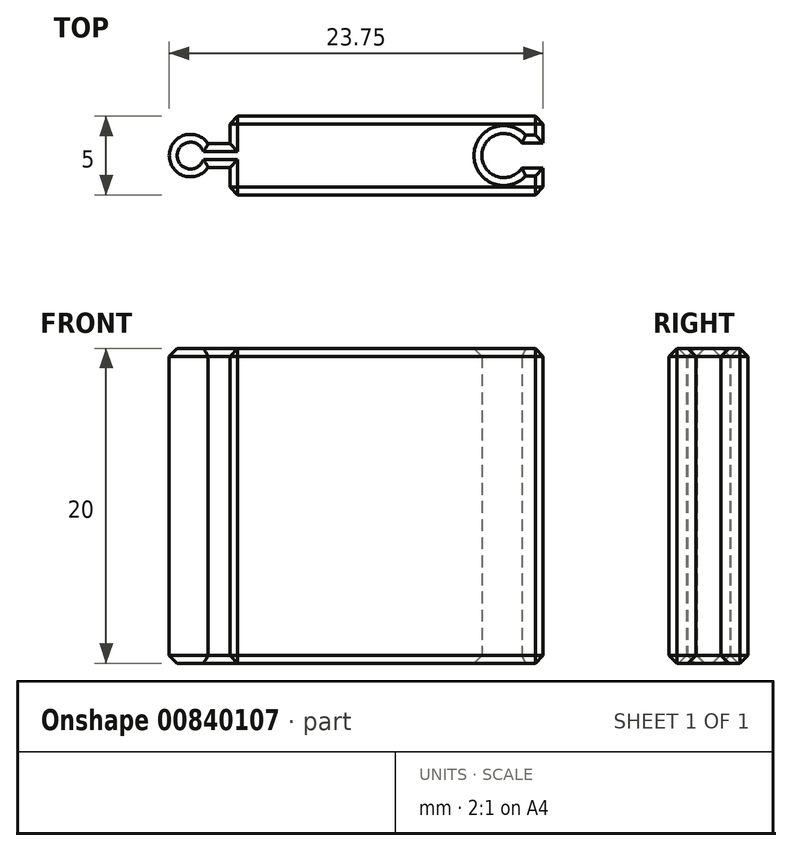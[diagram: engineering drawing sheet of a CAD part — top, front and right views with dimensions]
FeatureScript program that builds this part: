
annotation { "Feature Type Name" : "Feature", "Feature Type Description" : "" }
export const myFeature = defineFeature(function(context is Context, id is Id, definition is map)
    precondition{}
    {
        {
            var Q0;
            Q0=qCreatedBy(makeId("Top.planeOp"),FACE);
            var sketch = newSketch(context, id + "F0", { "sketchPlane" : qUnion([Q0])});
            skLineSegment(sketch, "E0.bottom", {"start": v(-9.95, 2.5) * mm, "end": v(9.95, 2.5) * mm});
            skLineSegment(sketch, "E0.top", {"start": v(-9.95, -2.5) * mm, "end": v(9.95, -2.5) * mm});
            skLineSegment(sketch, "E0.left", {"start": v(-9.95, 2.5) * mm, "end": v(-9.95, -2.5) * mm});
            skLineSegment(sketch, "E0.right", {"start": v(9.95, 2.5) * mm, "end": v(9.95, -2.5) * mm});
            skPoint(sketch, "E0.middle", {"position": v(0, 0) * mm});
            skLineSegment(sketch, "E1", {"start": v(-9.95, 0) * mm, "end": v(-12.45, 0) * mm});
            skCircle(sketch, "E2", {"center": v(-12.45, 0) * mm, "radius": 1.35 * mm});
            skLineSegment(sketch, "E3.bottom", {"start": v(-9.95, 0.75) * mm, "end": v(-12.45, 0.75) * mm});
            skLineSegment(sketch, "E3.top", {"start": v(-9.95, -0.75) * mm, "end": v(-12.45, -0.75) * mm});
            skLineSegment(sketch, "E3.left", {"start": v(-9.95, 0.75) * mm, "end": v(-9.95, -0.75) * mm});
            skLineSegment(sketch, "E3.right", {"start": v(-12.45, 0.75) * mm, "end": v(-12.45, -0.75) * mm});
            skPoint(sketch, "E3.middle", {"position": v(-11.2, 0) * mm});
            skLineSegment(sketch, "E4", {"start": v(9.95, 0) * mm, "end": v(7.45, 0) * mm});
            skCircle(sketch, "E5", {"center": v(7.45, 0) * mm, "radius": 1.4 * mm});
            skLineSegment(sketch, "E6.bottom", {"start": v(9.95, 0.8) * mm, "end": v(7.45, 0.8) * mm});
            skLineSegment(sketch, "E6.top", {"start": v(9.95, -0.8) * mm, "end": v(7.45, -0.8) * mm});
            skLineSegment(sketch, "E6.left", {"start": v(9.95, 0.8) * mm, "end": v(9.95, -0.8) * mm});
            skLineSegment(sketch, "E6.right", {"start": v(7.45, 0.8) * mm, "end": v(7.45, -0.8) * mm});
            skPoint(sketch, "E6.middle", {"position": v(8.7, 0) * mm});
            skSolve(sketch);
        }
        {
            var Q0;
            {var subQ10=sQuery(id+"F0.wireOp",EDGE,"E0.bottom");Q0=makeQuery(id+"F0.imprint","IMPRINT",FACE,{"disambiguationData":[TD([[makeQuery(id+"F0.imprint","IMPRINT",EDGE,{"derivedFrom":subQ10}),-1.0]])]});}
            var Q1;
            {var subQ0=sQuery(id+"F0.wireOp",EDGE,"E3.left");var subQ1=sQuery(id+"F0.wireOp",EDGE,"E1");var subQ2=makeQuery(id+"F0.imprint","INTERSECT",VERTEX,{"derivedFrom":[subQ1,subQ0]});Q1=makeQuery(id+"F0.imprint","IMPRINT",FACE,{"disambiguationData":[TD([[makeQuery(id+"F0.imprint","IMPRINT",EDGE,{"disambiguationData":[TD([[subQ2,-1.0]])],"derivedFrom":subQ1}),-1.0]])]});}
            var Q2;
            {var subQ0=sQuery(id+"F0.wireOp",EDGE,"E3.right");var subQ1=sQuery(id+"F0.wireOp",EDGE,"E1");var subQ2=makeQuery(id+"F0.imprint","INTERSECT",VERTEX,{"derivedFrom":[subQ1,subQ0]});Q2=makeQuery(id+"F0.imprint","IMPRINT",FACE,{"disambiguationData":[TD([[makeQuery(id+"F0.imprint","IMPRINT",EDGE,{"disambiguationData":[TD([[subQ2,1.0]])],"derivedFrom":subQ1}),1.0]])]});}
            var Q3;
            {var subQ0=sQuery(id+"F0.wireOp",EDGE,"E3.left");var subQ1=sQuery(id+"F0.wireOp",EDGE,"E1");var subQ2=makeQuery(id+"F0.imprint","INTERSECT",VERTEX,{"derivedFrom":[subQ1,subQ0]});Q3=makeQuery(id+"F0.imprint","IMPRINT",FACE,{"disambiguationData":[TD([[makeQuery(id+"F0.imprint","IMPRINT",EDGE,{"disambiguationData":[TD([[subQ2,-1.0]])],"derivedFrom":subQ1}),1.0]])]});}
            var Q4;
            {var subQ2=sQuery(id+"F0.wireOp",EDGE,"E3.bottom");var subQ4=sQuery(id+"F0.wireOp",EDGE,"E2");var subQ5=makeQuery(id+"F0.imprint","INTERSECT",VERTEX,{"derivedFrom":[subQ4,subQ2]});Q4=makeQuery(id+"F0.imprint","IMPRINT",FACE,{"disambiguationData":[TD([[makeQuery(id+"F0.imprint","IMPRINT",EDGE,{"disambiguationData":[TD([[subQ5,-1.0]])],"derivedFrom":subQ4}),1.0]])]});}
            var Q5;
            {var subQ0=sQuery(id+"F0.wireOp",EDGE,"E3.right");var subQ1=sQuery(id+"F0.wireOp",EDGE,"E1");var subQ2=makeQuery(id+"F0.imprint","INTERSECT",VERTEX,{"derivedFrom":[subQ1,subQ0]});Q5=makeQuery(id+"F0.imprint","IMPRINT",FACE,{"disambiguationData":[TD([[makeQuery(id+"F0.imprint","IMPRINT",EDGE,{"disambiguationData":[TD([[subQ2,1.0]])],"derivedFrom":subQ1}),-1.0]])]});}
            extrude(context, id + "F1", {"entities" : qUnion([Q0, Q1, Q2, Q3, Q4, Q5]), "depth" : 20 * mm, "offsetDistance" : 25 * mm});
        }
        {
            var Q0;
            Q0=makeQuery(id+"F1.opExtrude","CAP_EDGE",EDGE,{"disambiguationData":[OSD([sQuery(id+"F0.wireOp",EDGE,"E0.top")])],"isStart":false});
            var Q1;
            {var subQ0=sQuery(id+"F0.wireOp",EDGE,"E0.left");Q1=makeQuery(id+"F1.opExtrude","CAP_EDGE",EDGE,{"disambiguationData":[OSD([subQ0]),TDD([makeQuery(id+"F0.imprint","IMPRINT",EDGE,{"disambiguationData":[TD([[makeQuery(id+"F0.imprint","INTERSECT",VERTEX,{"derivedFrom":[sQuery(id+"F0.wireOp",EDGE,"E0.top"),subQ0]}),1.0]])],"derivedFrom":subQ0})])],"isStart":false});}
            var Q2;
            Q2=makeQuery(id+"F1.opExtrude","CAP_EDGE",EDGE,{"disambiguationData":[OSD([sQuery(id+"F0.wireOp",EDGE,"E3.top")])],"isStart":false});
            var Q3;
            Q3=makeQuery(id+"F1.opExtrude","CAP_EDGE",EDGE,{"disambiguationData":[OSD([sQuery(id+"F0.wireOp",EDGE,"E2")])],"isStart":false});
            var Q4;
            Q4=makeQuery(id+"F1.opExtrude","CAP_EDGE",EDGE,{"disambiguationData":[OSD([sQuery(id+"F0.wireOp",EDGE,"E3.bottom")])],"isStart":false});
            var Q5;
            {var subQ0=sQuery(id+"F0.wireOp",EDGE,"E0.left");Q5=makeQuery(id+"F1.opExtrude","CAP_EDGE",EDGE,{"disambiguationData":[OSD([subQ0]),TDD([makeQuery(id+"F0.imprint","IMPRINT",EDGE,{"disambiguationData":[TD([[makeQuery(id+"F0.imprint","INTERSECT",VERTEX,{"derivedFrom":[sQuery(id+"F0.wireOp",EDGE,"E0.bottom"),subQ0]}),-1.0]])],"derivedFrom":subQ0})])],"isStart":false});}
            var Q6;
            Q6=makeQuery(id+"F1.opExtrude","CAP_EDGE",EDGE,{"disambiguationData":[OSD([sQuery(id+"F0.wireOp",EDGE,"E0.bottom")])],"isStart":false});
            var Q7;
            {var subQ0=sQuery(id+"F0.wireOp",EDGE,"E0.right");Q7=makeQuery(id+"F1.opExtrude","CAP_EDGE",EDGE,{"disambiguationData":[OSD([subQ0]),TDD([makeQuery(id+"F0.imprint","IMPRINT",EDGE,{"disambiguationData":[TD([[makeQuery(id+"F0.imprint","INTERSECT",VERTEX,{"derivedFrom":[sQuery(id+"F0.wireOp",EDGE,"E0.bottom"),subQ0]}),-1.0]])],"derivedFrom":subQ0})])],"isStart":false});}
            var Q8;
            Q8=makeQuery(id+"F1.opExtrude","CAP_EDGE",EDGE,{"disambiguationData":[OSD([sQuery(id+"F0.wireOp",EDGE,"E6.bottom")])],"isStart":false});
            var Q9;
            Q9=makeQuery(id+"F1.opExtrude","CAP_EDGE",EDGE,{"disambiguationData":[OSD([sQuery(id+"F0.wireOp",EDGE,"E5")])],"isStart":false});
            var Q10;
            Q10=makeQuery(id+"F1.opExtrude","CAP_EDGE",EDGE,{"disambiguationData":[OSD([sQuery(id+"F0.wireOp",EDGE,"E6.top")])],"isStart":false});
            var Q11;
            {var subQ0=sQuery(id+"F0.wireOp",EDGE,"E0.right");Q11=makeQuery(id+"F1.opExtrude","CAP_EDGE",EDGE,{"disambiguationData":[OSD([subQ0]),TDD([makeQuery(id+"F0.imprint","IMPRINT",EDGE,{"disambiguationData":[TD([[makeQuery(id+"F0.imprint","INTERSECT",VERTEX,{"derivedFrom":[sQuery(id+"F0.wireOp",EDGE,"E0.top"),subQ0]}),1.0]])],"derivedFrom":subQ0})])],"isStart":false});}
            var Q12;
            Q12=makeQuery(id+"F1.opExtrude","SWEPT_EDGE",EDGE,{"disambiguationData":[OSD([sQuery(id+"F0.wireOp",EDGE,"E0.top"),sQuery(id+"F0.wireOp",EDGE,"E0.right")])]});
            var Q13;
            Q13=makeQuery(id+"F1.opExtrude","SWEPT_EDGE",EDGE,{"disambiguationData":[OSD([sQuery(id+"F0.wireOp",EDGE,"E0.bottom"),sQuery(id+"F0.wireOp",EDGE,"E0.right")])]});
            var Q14;
            Q14=makeQuery(id+"F1.opExtrude","SWEPT_EDGE",EDGE,{"disambiguationData":[OSD([sQuery(id+"F0.wireOp",EDGE,"E0.top"),sQuery(id+"F0.wireOp",EDGE,"E0.left")])]});
            var Q15;
            Q15=makeQuery(id+"F1.opExtrude","SWEPT_EDGE",EDGE,{"disambiguationData":[OSD([sQuery(id+"F0.wireOp",EDGE,"E0.bottom"),sQuery(id+"F0.wireOp",EDGE,"E0.left")])]});
            var Q16;
            Q16=makeQuery(id+"F1.opExtrude","CAP_EDGE",EDGE,{"disambiguationData":[OSD([sQuery(id+"F0.wireOp",EDGE,"E0.top")])],"isStart":true});
            var Q17;
            {var subQ0=sQuery(id+"F0.wireOp",EDGE,"E0.right");Q17=makeQuery(id+"F1.opExtrude","CAP_EDGE",EDGE,{"disambiguationData":[OSD([subQ0]),TDD([makeQuery(id+"F0.imprint","IMPRINT",EDGE,{"disambiguationData":[TD([[makeQuery(id+"F0.imprint","INTERSECT",VERTEX,{"derivedFrom":[sQuery(id+"F0.wireOp",EDGE,"E0.top"),subQ0]}),1.0]])],"derivedFrom":subQ0})])],"isStart":true});}
            var Q18;
            Q18=makeQuery(id+"F1.opExtrude","CAP_EDGE",EDGE,{"disambiguationData":[OSD([sQuery(id+"F0.wireOp",EDGE,"E6.top")])],"isStart":true});
            var Q19;
            Q19=makeQuery(id+"F1.opExtrude","CAP_EDGE",EDGE,{"disambiguationData":[OSD([sQuery(id+"F0.wireOp",EDGE,"E5")])],"isStart":true});
            var Q20;
            Q20=makeQuery(id+"F1.opExtrude","CAP_EDGE",EDGE,{"disambiguationData":[OSD([sQuery(id+"F0.wireOp",EDGE,"E6.bottom")])],"isStart":true});
            var Q21;
            {var subQ0=sQuery(id+"F0.wireOp",EDGE,"E0.right");Q21=makeQuery(id+"F1.opExtrude","CAP_EDGE",EDGE,{"disambiguationData":[OSD([subQ0]),TDD([makeQuery(id+"F0.imprint","IMPRINT",EDGE,{"disambiguationData":[TD([[makeQuery(id+"F0.imprint","INTERSECT",VERTEX,{"derivedFrom":[sQuery(id+"F0.wireOp",EDGE,"E0.bottom"),subQ0]}),-1.0]])],"derivedFrom":subQ0})])],"isStart":true});}
            var Q22;
            Q22=makeQuery(id+"F1.opExtrude","CAP_EDGE",EDGE,{"disambiguationData":[OSD([sQuery(id+"F0.wireOp",EDGE,"E0.bottom")])],"isStart":true});
            var Q23;
            {var subQ0=sQuery(id+"F0.wireOp",EDGE,"E0.left");Q23=makeQuery(id+"F1.opExtrude","CAP_EDGE",EDGE,{"disambiguationData":[OSD([subQ0]),TDD([makeQuery(id+"F0.imprint","IMPRINT",EDGE,{"disambiguationData":[TD([[makeQuery(id+"F0.imprint","INTERSECT",VERTEX,{"derivedFrom":[sQuery(id+"F0.wireOp",EDGE,"E0.bottom"),subQ0]}),-1.0]])],"derivedFrom":subQ0})])],"isStart":true});}
            var Q24;
            Q24=makeQuery(id+"F1.opExtrude","CAP_EDGE",EDGE,{"disambiguationData":[OSD([sQuery(id+"F0.wireOp",EDGE,"E3.bottom")])],"isStart":true});
            var Q25;
            Q25=makeQuery(id+"F1.opExtrude","CAP_EDGE",EDGE,{"disambiguationData":[OSD([sQuery(id+"F0.wireOp",EDGE,"E3.top")])],"isStart":true});
            var Q26;
            {var subQ0=sQuery(id+"F0.wireOp",EDGE,"E0.left");Q26=makeQuery(id+"F1.opExtrude","CAP_EDGE",EDGE,{"disambiguationData":[OSD([subQ0]),TDD([makeQuery(id+"F0.imprint","IMPRINT",EDGE,{"disambiguationData":[TD([[makeQuery(id+"F0.imprint","INTERSECT",VERTEX,{"derivedFrom":[sQuery(id+"F0.wireOp",EDGE,"E0.top"),subQ0]}),1.0]])],"derivedFrom":subQ0})])],"isStart":true});}
            var Q27;
            Q27=makeQuery(id+"F1.opExtrude","CAP_EDGE",EDGE,{"disambiguationData":[OSD([sQuery(id+"F0.wireOp",EDGE,"E2")])],"isStart":true});
            chamfer(context, id + "F2", {"entities" : qUnion([Q0, Q1, Q2, Q3, Q4, Q5, Q6, Q7, Q8, Q9, Q10, Q11, Q12, Q13, Q14, Q15, Q16, Q17, Q18, Q19, Q20, Q21, Q22, Q23, Q24, Q25, Q26, Q27]), "width" : .5 * mm, "tangentPropagation" : true});
        }
    });
